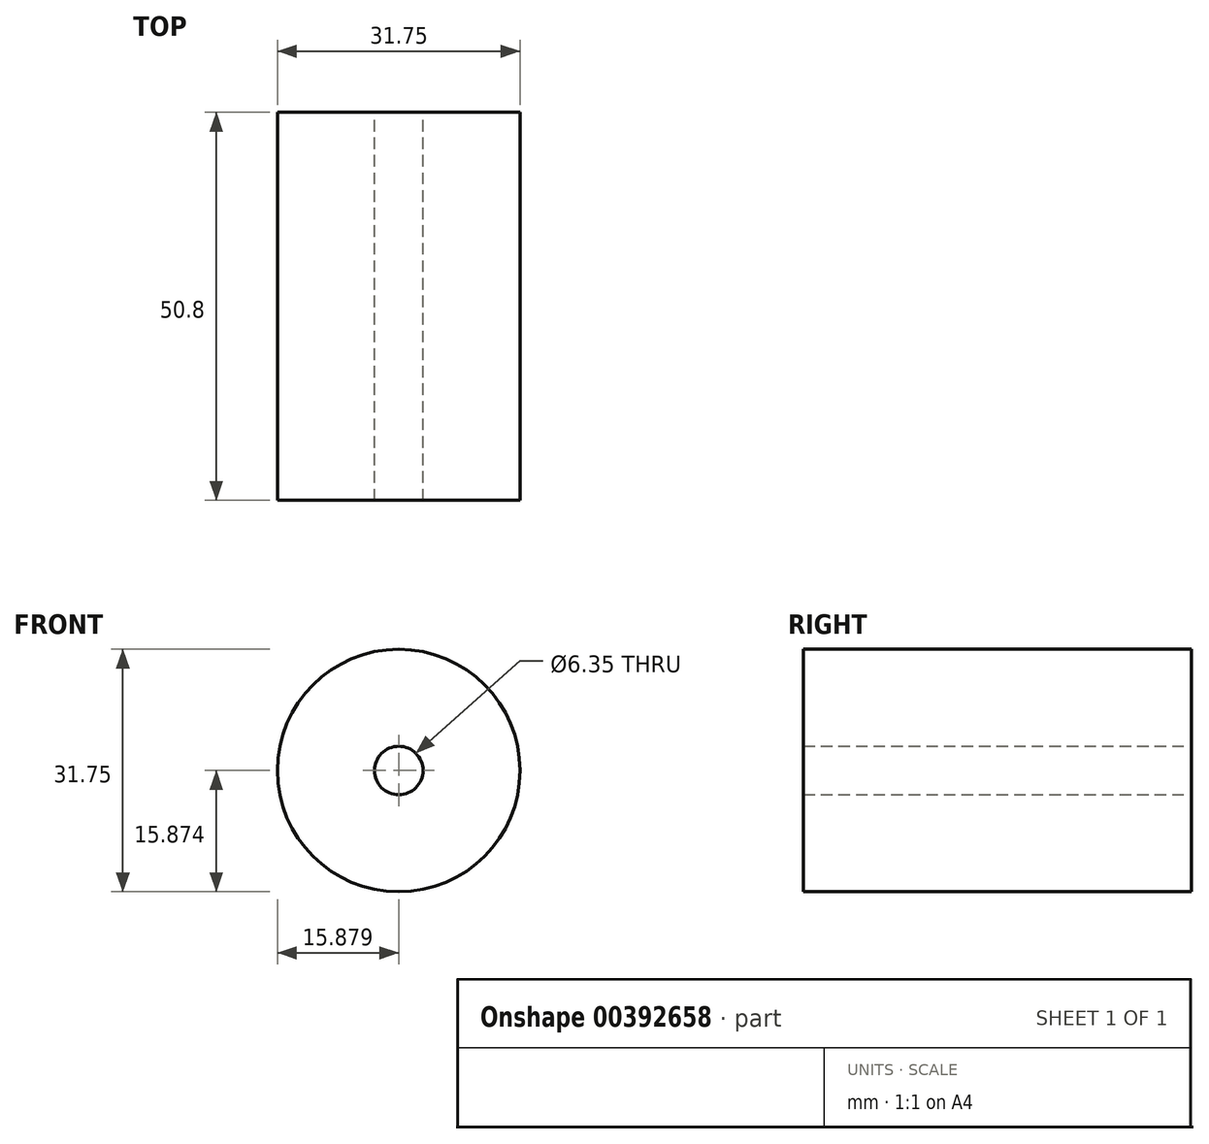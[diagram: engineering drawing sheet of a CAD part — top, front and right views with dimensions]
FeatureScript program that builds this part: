
annotation { "Feature Type Name" : "Feature", "Feature Type Description" : "" }
export const myFeature = defineFeature(function(context is Context, id is Id, definition is map)
    precondition{}
    {
        {
            var Q0;
            Q0=qCreatedBy(makeId("Front.planeOp"),FACE);
            var sketch = newSketch(context, id + "F0", { "sketchPlane" : qUnion([Q0])});
            skPoint(sketch, "E0", {"position": v(19.94, 20.44) * mm});
            skCircle(sketch, "E1", {"center": v(19.94, 20.44) * mm, "radius": 15.88 * mm});
            skSolve(sketch);
        }
        {
            var Q0;
            Q0=makeQuery(id+"F0.imprint","IMPRINT",FACE,{"disambiguationData":[TD([[makeQuery(id+"F0.imprint","IMPRINT",EDGE,{"derivedFrom":sQuery(id+"F0.wireOp",EDGE,"E1")}),1.0]])]});
            extrude(context, id + "F1", {"entities" : qUnion([Q0]), "depth" : 50.8 * mm});
        }
        {
            var Q0;
            Q0=sQuery(id+"F0.wireOp",VERTEX,"E0");
            var Q1;
            Q1=makeQuery(id+"F1.opExtrude","SWEPT_BODY",BODY,{"disambiguationData":[OSD([sQuery(id+"F0.wireOp",EDGE,"E1")])]});
            hole(context, id + "F2", {"style" : HoleStyle.SIMPLE, "endStyle" : HoleEndStyle.THROUGH, "oppositeDirection" : true, "holeDiameter" : 6.35 * mm, "isTappedThrough" : true, "tappedDepth" : 12.7 * mm, "tapClearance" : 3, "locations" : qUnion([Q0]), "scope" : qUnion([Q1])});
        }
    });
